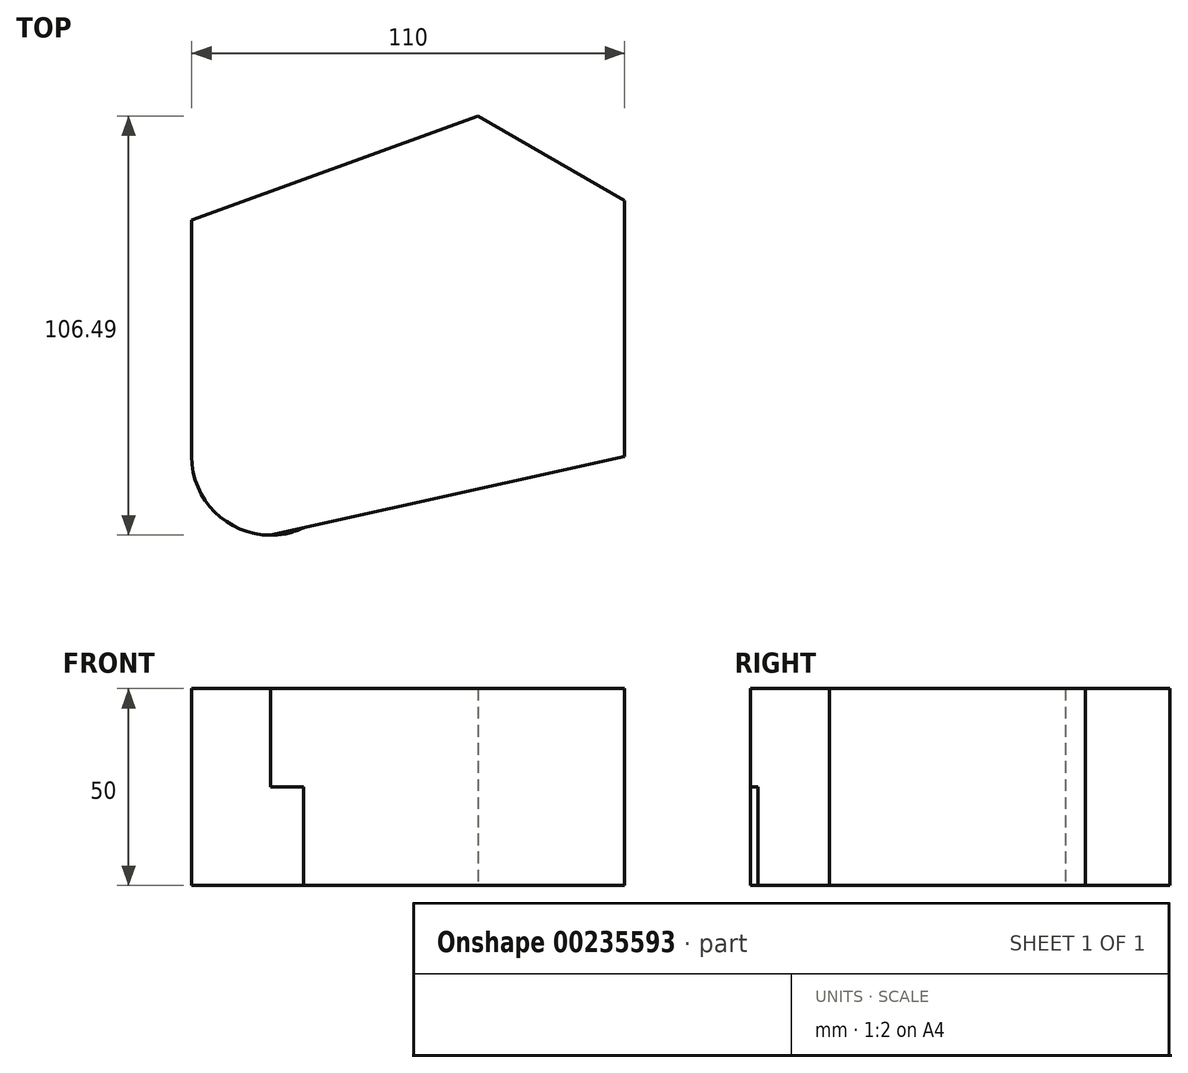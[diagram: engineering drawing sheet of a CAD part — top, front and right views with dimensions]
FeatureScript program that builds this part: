
annotation { "Feature Type Name" : "Feature", "Feature Type Description" : "" }
export const myFeature = defineFeature(function(context is Context, id is Id, definition is map)
    precondition{}
    {
        {
            var Q0;
            Q0=qCreatedBy(makeId("Top.planeOp"),FACE);
            var sketch = newSketch(context, id + "F0", { "sketchPlane" : qUnion([Q0])});
            skLineSegment(sketch, "E0", {"start": v(70.45, 33.3) * mm, "end": v(70.45, -31.7) * mm});
            skArc(sketch, "E1", {"start": v(-39.55, -31.7) * mm, "mid": v(-30.29, -48.57) * mm, "end": v(-11.08, -49.8) * mm});
            skLineSegment(sketch, "E2", {"start": v(-39.55, -31.7) * mm, "end": v(-39.55, 28.3) * mm});
            skLineSegment(sketch, "E3", {"start": v(70.45, -31.7) * mm, "end": v(-19.55, -51.7) * mm});
            skLineSegment(sketch, "E4", {"start": v(-39.55, 28.3) * mm, "end": v(-5.78, 28.3) * mm});
            skLineSegment(sketch, "E5", {"start": v(-39.55, 28.3) * mm, "end": v(33.23, 54.8) * mm});
            skLineSegment(sketch, "E6", {"start": v(70.45, 33.3) * mm, "end": v(44.1, 33.3) * mm});
            skLineSegment(sketch, "E7", {"start": v(70.45, 33.3) * mm, "end": v(33.23, 54.8) * mm});
            skPoint(sketch, "E8", {"position": v(33.23, 54.8) * mm});
            skSolve(sketch);
        }
        {
            var Q0;
            {var subQ1=sQuery(id+"F0.wireOp",EDGE,"E0");Q0=makeQuery(id+"F0.imprint","IMPRINT",FACE,{"disambiguationData":[TD([[makeQuery(id+"F0.imprint","IMPRINT",EDGE,{"derivedFrom":subQ1}),-1.0]])]});}
            extrude(context, id + "F1", {"entities" : qUnion([Q0]), "depth" : 25 * mm});
        }
        {
            var Q0;
            Q0 = qSketchRegion(id + "F0", true);
            var Q1;
            Q1=makeQuery(id+"F1.opExtrude","CAP_FACE",FACE,{"disambiguationData":[OSD([sQuery(id+"F0.wireOp",EDGE,"E0"),sQuery(id+"F0.wireOp",EDGE,"E1"),sQuery(id+"F0.wireOp",EDGE,"E2"),sQuery(id+"F0.wireOp",EDGE,"E3"),sQuery(id+"F0.wireOp",EDGE,"E5"),sQuery(id+"F0.wireOp",EDGE,"E7")])],"isStart":false});
            extrude(context, id + "F2", {"entities" : qUnion([Q0, Q1]), "operationType" : NewBodyOperationType.ADD, "depth" : 25 * mm});
        }
    });
